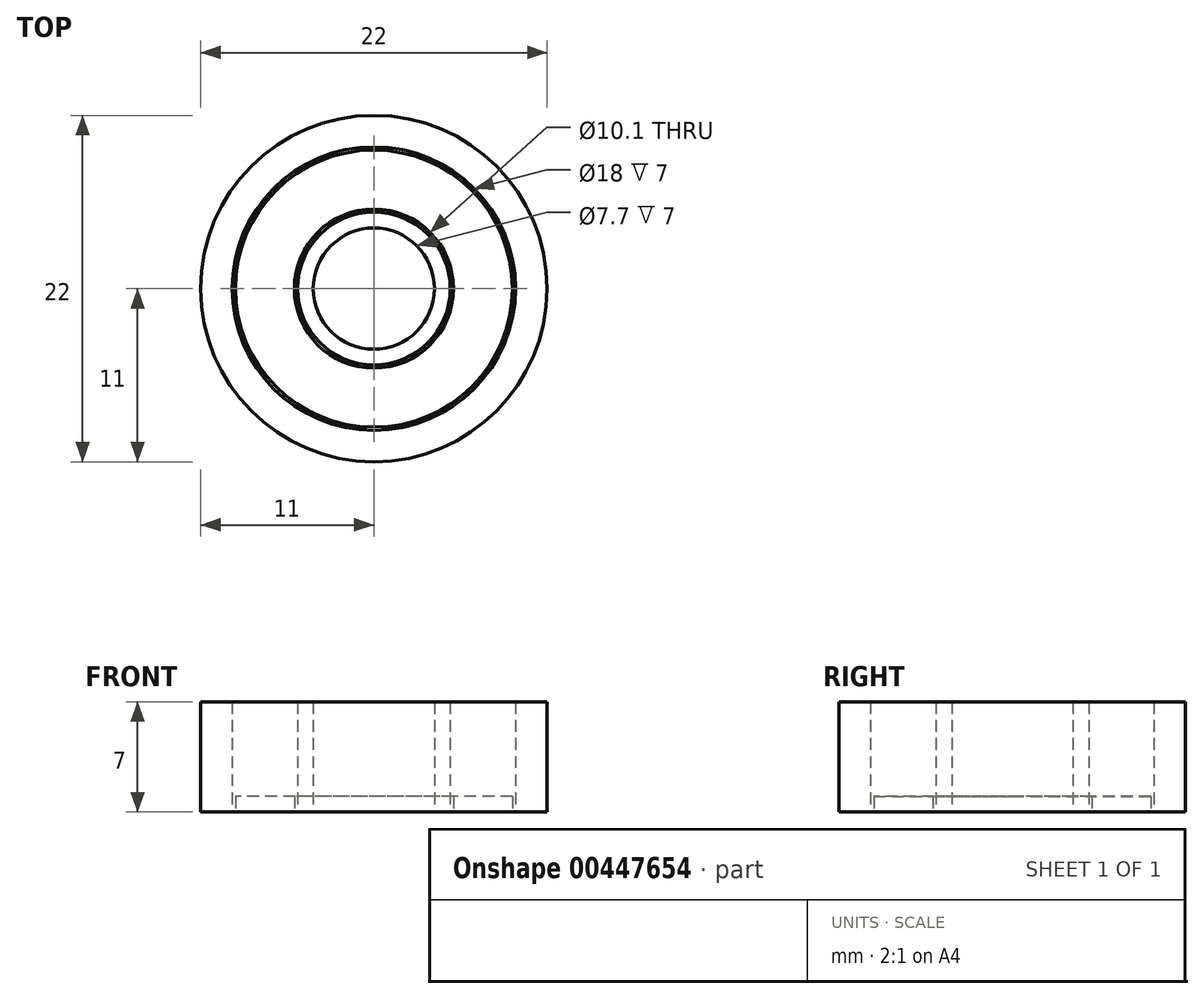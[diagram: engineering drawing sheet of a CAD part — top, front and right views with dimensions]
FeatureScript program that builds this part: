
annotation { "Feature Type Name" : "Feature", "Feature Type Description" : "" }
export const myFeature = defineFeature(function(context is Context, id is Id, definition is map)
    precondition{}
    {
        {
            var Q0;
            Q0=qCreatedBy(makeId("Top.planeOp"),FACE);
            var sketch = newSketch(context, id + "F0", { "sketchPlane" : qUnion([Q0])});
            skCircle(sketch, "E0", {"center": v(0, 0) * mm, "radius": 4.85 * mm});
            skCircle(sketch, "E1", {"center": v(0, 0) * mm, "radius": 3.85 * mm});
            skSolve(sketch);
        }
        {
            var Q0;
            Q0=makeQuery(id+"F0.imprint","IMPRINT",FACE,{"disambiguationData":[TD([[makeQuery(id+"F0.imprint","IMPRINT",EDGE,{"derivedFrom":sQuery(id+"F0.wireOp",EDGE,"E0")}),1.0]])]});
            extrude(context, id + "F1", {"entities" : qUnion([Q0]), "depth" : 7 * mm, "offsetDistance" : 25 * mm});
        }
        {
            var Q0;
            Q0=qCreatedBy(makeId("Top.planeOp"),FACE);
            var sketch = newSketch(context, id + "F2", { "sketchPlane" : qUnion([Q0])});
            skCircle(sketch, "E2", {"center": v(0, 0) * mm, "radius": 9 * mm});
            skCircle(sketch, "E3", {"center": v(0, 0) * mm, "radius": 11 * mm});
            skSolve(sketch);
        }
        {
            var Q0;
            Q0=makeQuery(id+"F2.imprint","IMPRINT",FACE,{"disambiguationData":[TD([[makeQuery(id+"F2.imprint","IMPRINT",EDGE,{"derivedFrom":sQuery(id+"F2.wireOp",EDGE,"E2")}),-1.0]])]});
            extrude(context, id + "F3", {"entities" : qUnion([Q0]), "depth" : 7 * mm, "offsetDistance" : 25 * mm});
        }
        {
            var Q0;
            Q0=qCreatedBy(makeId("Top.planeOp"),FACE);
            var sketch = newSketch(context, id + "F4", { "sketchPlane" : qUnion([Q0])});
            skCircle(sketch, "E4", {"center": v(0, 0) * mm, "radius": 8.8 * mm});
            skCircle(sketch, "E5", {"center": v(0, 0) * mm, "radius": 5.05 * mm});
            skSolve(sketch);
        }
        {
            var Q0;
            Q0=makeQuery(id+"F4.imprint","IMPRINT",FACE,{"disambiguationData":[TD([[makeQuery(id+"F4.imprint","IMPRINT",EDGE,{"derivedFrom":sQuery(id+"F4.wireOp",EDGE,"E4")}),1.0]])]});
            extrude(context, id + "F5", {"entities" : qUnion([Q0]), "depth" : 1 * mm, "offsetDistance" : 25 * mm});
        }
    });
